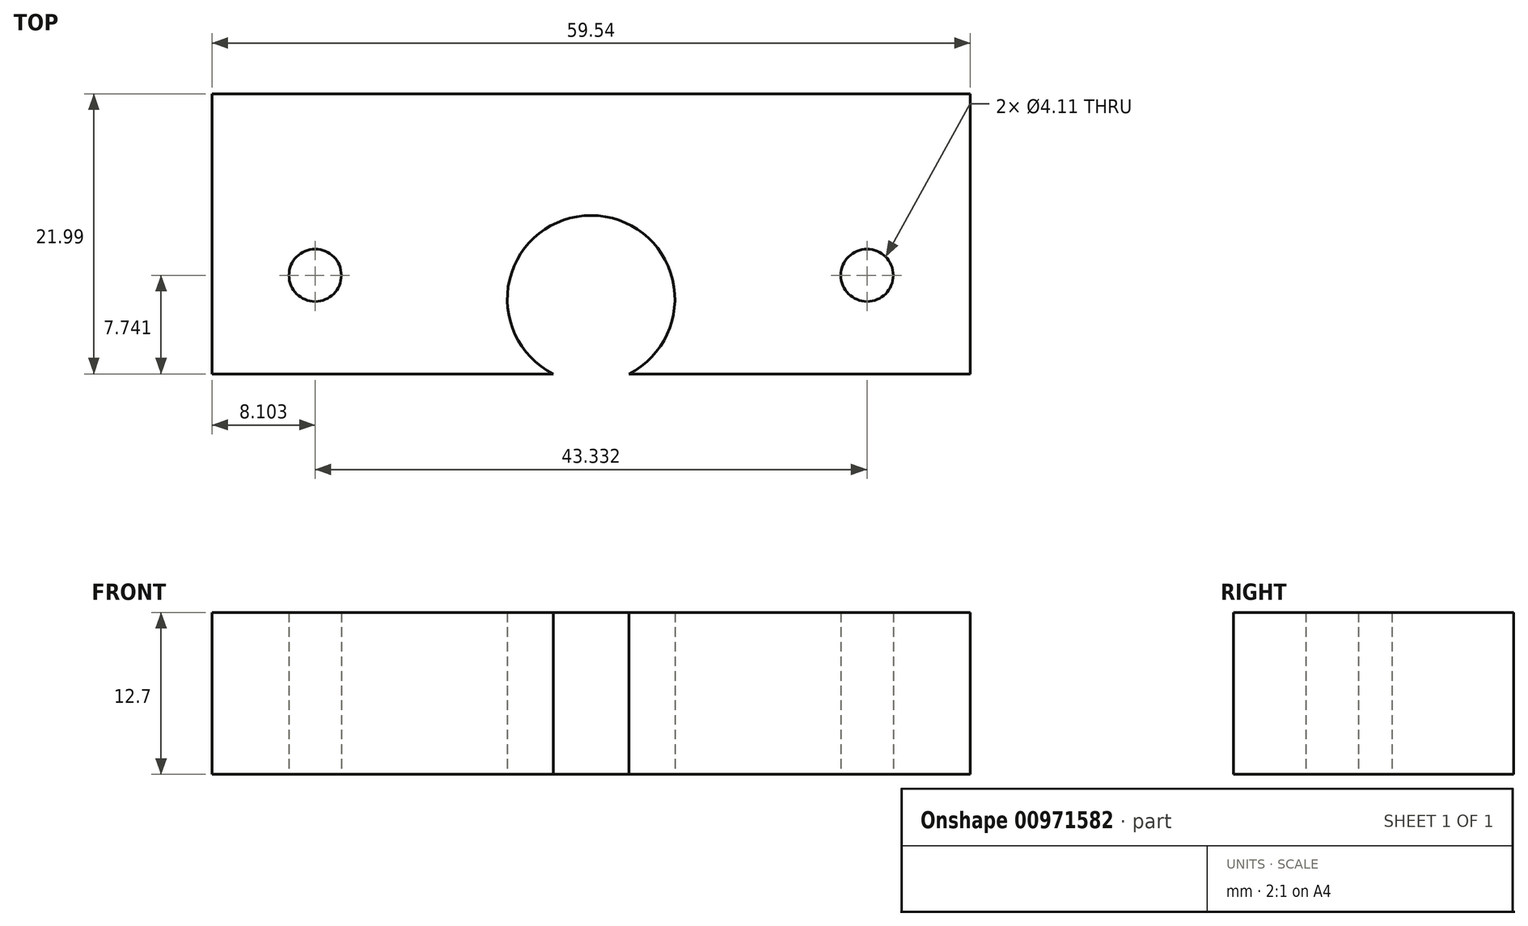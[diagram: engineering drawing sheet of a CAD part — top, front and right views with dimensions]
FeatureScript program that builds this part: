
annotation { "Feature Type Name" : "Feature", "Feature Type Description" : "" }
export const myFeature = defineFeature(function(context is Context, id is Id, definition is map)
    precondition{}
    {
        {
            var Q0;
            Q0=qCreatedBy(makeId("Top.planeOp"),FACE);
            var sketch = newSketch(context, id + "F0", { "sketchPlane" : qUnion([Q0])});
            skLineSegment(sketch, "E0.bottom", {"start": v(0, -13.02) * mm, "end": v(59.54, -13.02) * mm});
            skLineSegment(sketch, "E0.left", {"start": v(0, -13.02) * mm, "end": v(0, 8.97) * mm});
            skLineSegment(sketch, "E0.right", {"start": v(59.54, -13.02) * mm, "end": v(59.54, 8.97) * mm});
            skArc(sketch, "E1", {"start": v(32.75, -13.02) * mm, "mid": v(29.77, -0.58) * mm, "end": v(26.8, -13.02) * mm});
            skLineSegment(sketch, "E2", {"start": v(0, 8.97) * mm, "end": v(59.54, 8.97) * mm});
            skCircle(sketch, "E3", {"center": v(51.44, -5.28) * mm, "radius": 2.06 * mm});
            skLineSegment(sketch, "E4", {"start": v(29.77, -7.16) * mm, "end": v(29.77, 13.78) * mm, "construction": true});
            skCircle(sketch, "E5.MirrorC", {"center": v(8.1, -5.28) * mm, "radius": 2.06 * mm});
            skSolve(sketch);
        }
        {
            var Q0;
            {var subQ6=sQuery(id+"F0.wireOp",EDGE,"E1");Q0=makeQuery(id+"F0.imprint","IMPRINT",FACE,{"disambiguationData":[TD([[makeQuery(id+"F0.imprint","IMPRINT",EDGE,{"derivedFrom":subQ6}),-1.0]])]});}
            var Q1;
            {var subQ0=sQuery(id+"F0.wireOp",EDGE,"E0.top");Q1=makeQuery(id+"F0.imprint","IMPRINT",FACE,{"disambiguationData":[TD([[makeQuery(id+"F0.imprint","IMPRINT",EDGE,{"derivedFrom":subQ0}),-1.0]])]});}
            extrude(context, id + "F1", {"entities" : qUnion([Q0, Q1]), "depth" : 12.7 * mm, "offsetDistance" : 25.4 * mm});
        }
    });
